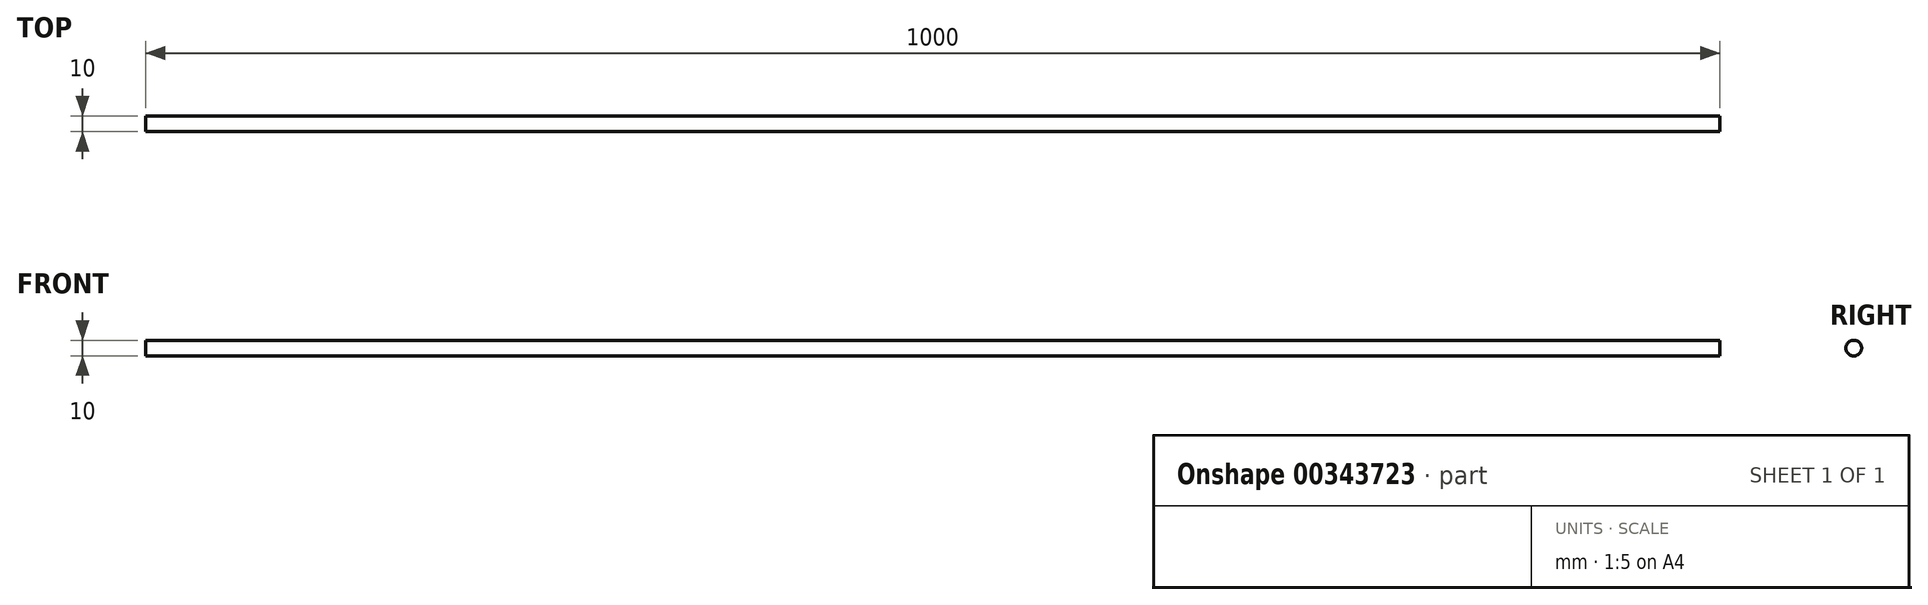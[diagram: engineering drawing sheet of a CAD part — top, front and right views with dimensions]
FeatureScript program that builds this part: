
annotation { "Feature Type Name" : "Feature", "Feature Type Description" : "" }
export const myFeature = defineFeature(function(context is Context, id is Id, definition is map)
    precondition{}
    {
        {
            var Q0;
            Q0=qCreatedBy(makeId("Right.planeOp"),FACE);
            var sketch = newSketch(context, id + "F0", { "sketchPlane" : qUnion([Q0])});
            skCircle(sketch, "E0", {"center": v(0, 0) * mm, "radius": 5 * mm});
            skSolve(sketch);
        }
        {
            var Q0;
            Q0 = qSketchRegion(id + "F0", true);
            extrude(context, id + "F1", {"entities" : qUnion([Q0]), "depth" : 1000 * mm, "symmetric" : true});
        }
    });
